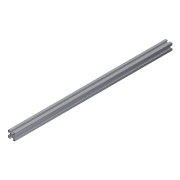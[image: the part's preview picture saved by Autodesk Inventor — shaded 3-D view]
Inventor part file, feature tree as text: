
AUTODESK INVENTOR PART (.ipt)
format: ipt  version: 2011 (Build 150239000, 239)  size: 169,472 bytes
history: native  units: in
note: dims shown in document units (in); Inventor stores cm internally (conversion verified against a paired STEP export)
features: extrude x1, sketch x1
ambient origin geometry x8: Origin, YZ Plane, XZ Plane, XY Plane, X Axis, Y Axis, Z Axis, Center Point
bodies: Solid1 (feature_tree)
feature tree (2):
  extrude  "Extrusion1"  [1 undecoded]
  sketch  "Sketch1"  dims[d0=17.5in d1=0.0in]
note: 1 required parameter value undecoded (feature->parameter linkage not recoverable at this tier; creation-order binding heuristic only, values carry confidence <= 0.55)
